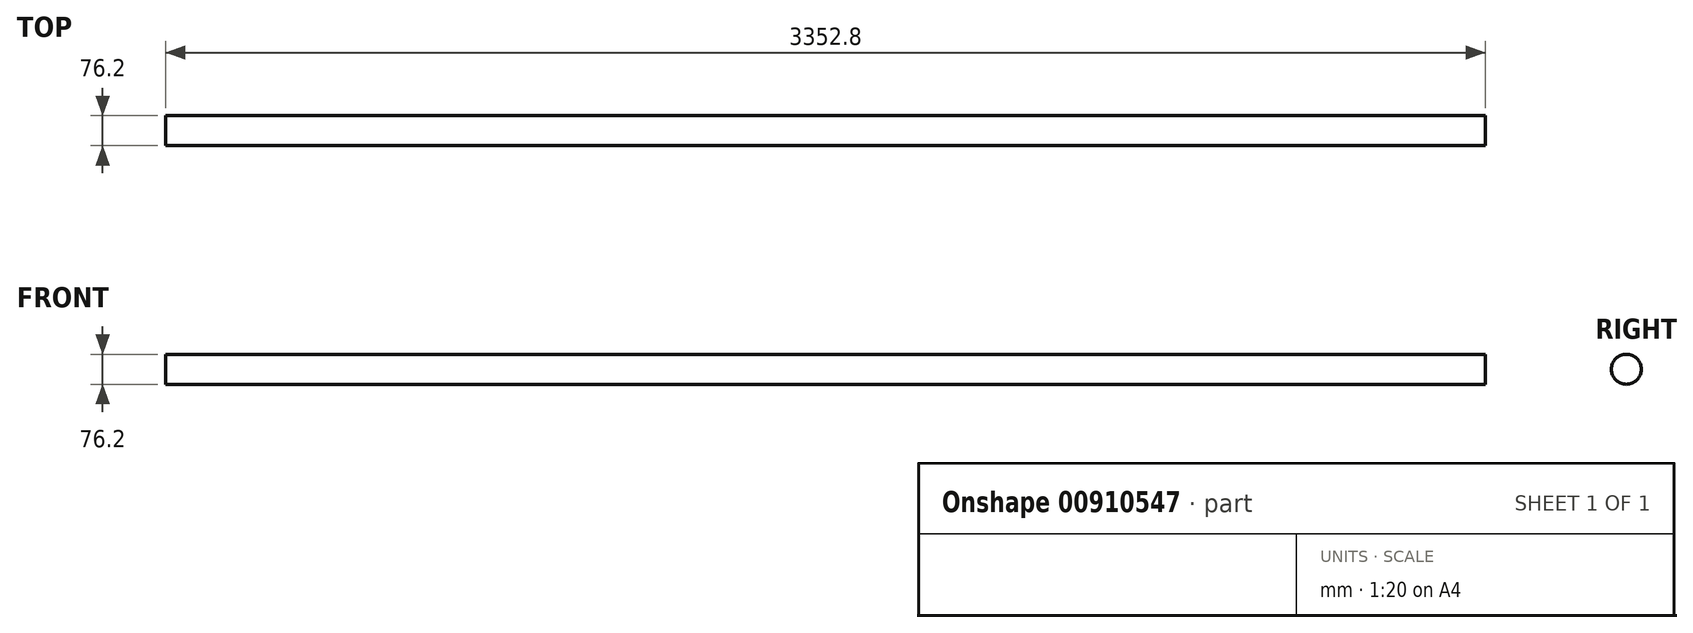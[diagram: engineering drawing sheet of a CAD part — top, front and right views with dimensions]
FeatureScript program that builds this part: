
annotation { "Feature Type Name" : "Feature", "Feature Type Description" : "" }
export const myFeature = defineFeature(function(context is Context, id is Id, definition is map)
    precondition{}
    {
        {
            var Q0;
            Q0=qCreatedBy(makeId("Top.planeOp"),FACE);
            var sketch = newSketch(context, id + "F0", { "sketchPlane" : qUnion([Q0])});
            skLineSegment(sketch, "E0", {"start": v(-1986.68, -38.1) * mm, "end": v(1366.12, -38.1) * mm});
            skLineSegment(sketch, "E1", {"start": v(1366.12, -38.1) * mm, "end": v(1366.12, 0) * mm});
            skLineSegment(sketch, "E2", {"start": v(1366.12, 0) * mm, "end": v(-1986.68, 0) * mm});
            skLineSegment(sketch, "E3", {"start": v(-1986.68, 0) * mm, "end": v(-1986.68, -38.1) * mm});
            skSolve(sketch);
        }
        {
            var Q0;
            Q0=makeQuery(id+"F0.imprint","IMPRINT",FACE,{"disambiguationData":[TD([[makeQuery(id+"F0.imprint","IMPRINT",EDGE,{"derivedFrom":sQuery(id+"F0.wireOp",EDGE,"E0")}),1.0]])]});
            var Q1;
            Q1=sQuery(id+"F0.wireOp",EDGE,"E0");
            revolve(context, id + "F1", {"surfaceOperationType" : NewSurfaceOperationType.NEW, "entities" : qUnion([Q0]), "axis" : qUnion([Q1]), "revolveType" : RevolveType.FULL});
        }
    });
